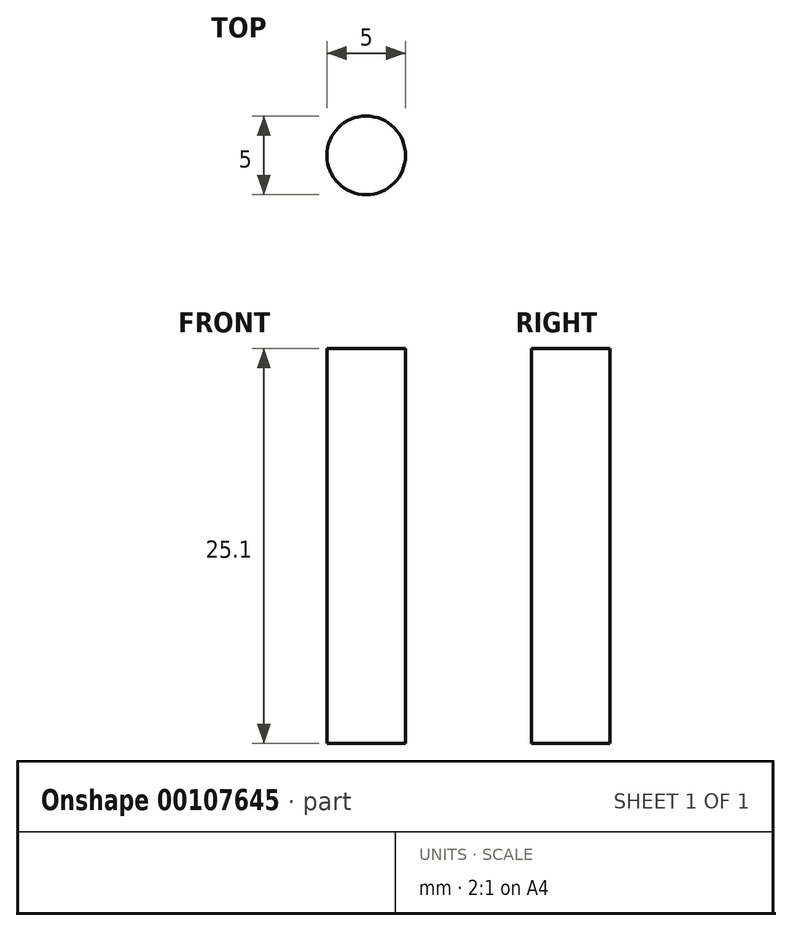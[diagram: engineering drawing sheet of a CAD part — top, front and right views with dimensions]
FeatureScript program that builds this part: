
annotation { "Feature Type Name" : "Feature", "Feature Type Description" : "" }
export const myFeature = defineFeature(function(context is Context, id is Id, definition is map)
    precondition{}
    {
        {
            var Q0;
            Q0=qCreatedBy(makeId("Top.planeOp"),FACE);
            var sketch = newSketch(context, id + "F0", { "sketchPlane" : qUnion([Q0])});
            skCircle(sketch, "E0", {"center": v(0, 0) * mm, "radius": 2.5 * mm});
            skSolve(sketch);
        }
        {
            var Q0;
            Q0=sQuery(id+"F0.wireOp",EDGE,"E0");
            extrude(context, id + "F1", {"bodyType" : ToolBodyType.SURFACE, "surfaceEntities" : qUnion([Q0]), "depth" : 25.1 * mm});
        }
    });
